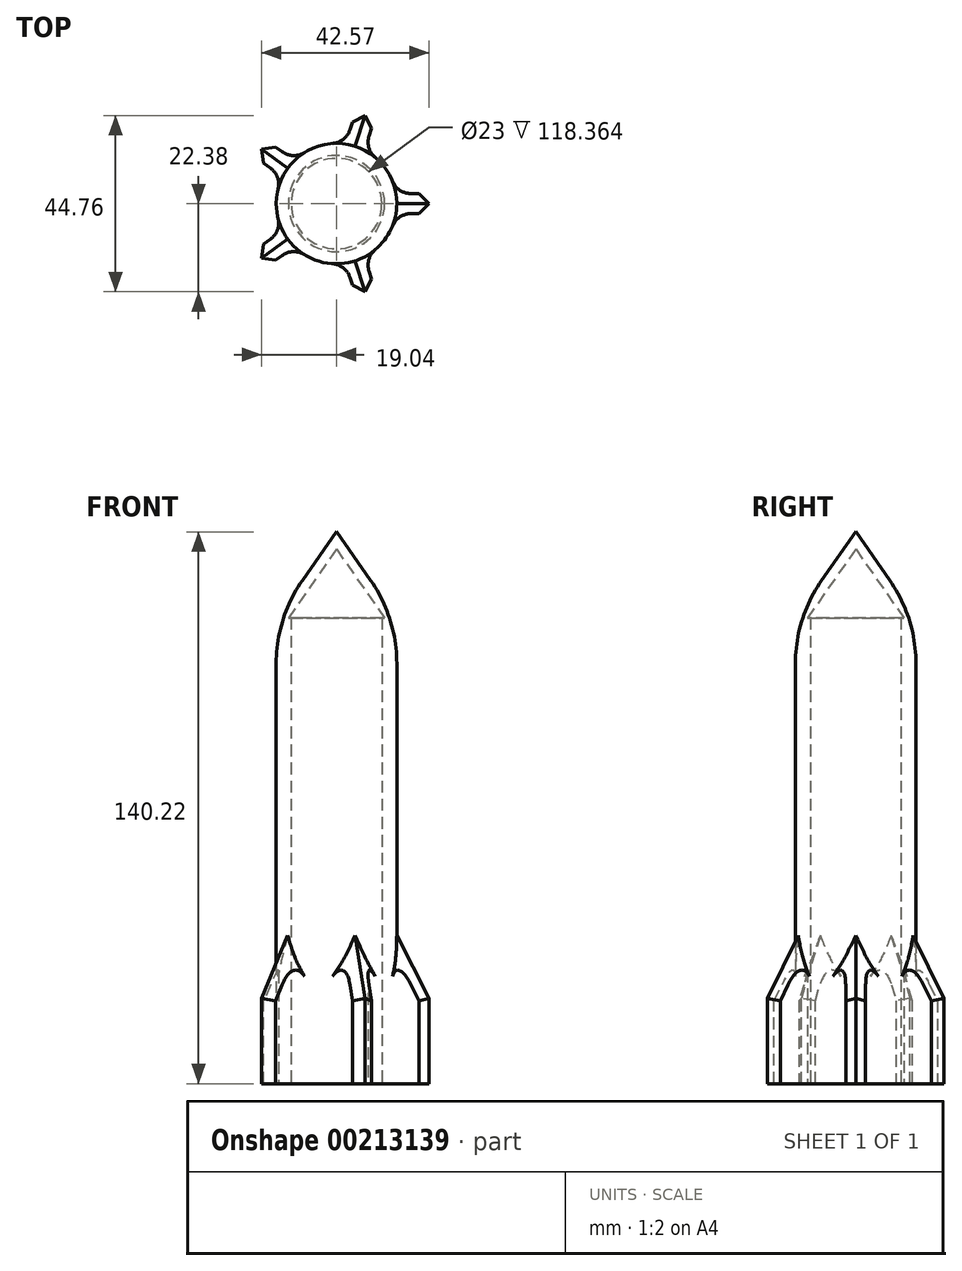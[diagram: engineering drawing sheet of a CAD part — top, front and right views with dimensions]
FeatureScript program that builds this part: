
annotation { "Feature Type Name" : "Feature", "Feature Type Description" : "" }
export const myFeature = defineFeature(function(context is Context, id is Id, definition is map)
    precondition{}
    {
        {
            var Q0;
            Q0=qCreatedBy(makeId("Top.planeOp"),FACE);
            var sketch = newSketch(context, id + "F0", { "sketchPlane" : qUnion([Q0])});
            skCircle(sketch, "E0", {"center": v(0, 0) * mm, "radius": 11.5 * mm});
            skCircle(sketch, "E1", {"center": v(0, 0) * mm, "radius": 15.3 * mm});
            skSolve(sketch);
        }
        {
            var Q0;
            Q0=makeQuery(id+"F0.imprint","IMPRINT",FACE,{"disambiguationData":[TD([[makeQuery(id+"F0.imprint","IMPRINT",EDGE,{"derivedFrom":sQuery(id+"F0.wireOp",EDGE,"E0")}),-1.0]])]});
            extrude(context, id + "F1", {"entities" : qUnion([Q0]), "depth" : 101.6 * mm});
        }
        {
            var Q0;
            Q0=makeQuery(id+"F1.opExtrude","CAP_FACE",FACE,{"disambiguationData":[OSD([sQuery(id+"F0.wireOp",EDGE,"E0"),sQuery(id+"F0.wireOp",EDGE,"E1")])],"isStart":false});
            extrude(context, id + "F2", {"entities" : qUnion([Q0]), "operationType" : NewBodyOperationType.ADD, "depth" : 25.4 * mm});
        }
        {
            var Q0;
            Q0=makeQuery(id+"F2.opExtrude","CAP_FACE",FACE,{"disambiguationData":[OSD([sQuery(id+"F0.wireOp",EDGE,"E0"),sQuery(id+"F0.wireOp",EDGE,"E1")])],"isStart":false});
            extrude(context, id + "F3", {"entities" : qUnion([Q0]), "operationType" : NewBodyOperationType.REMOVE, "oppositeDirection" : true, "depth" : 25.4 * mm});
        }
        {
            var Q0;
            Q0=makeQuery(id+"F3.boolean.opBoolean","COPY",FACE,{"derivedFrom":makeQuery(id+"F3.opExtrude","CAP_FACE",FACE,{"disambiguationData":[OSD([sQuery(id+"F0.wireOp",EDGE,"E0"),sQuery(id+"F0.wireOp",EDGE,"E1")])],"isStart":false})});
            extrude(context, id + "F4", {"entities" : qUnion([Q0]), "operationType" : NewBodyOperationType.ADD, "depth" : 25.4 * mm});
        }
        {
            var Q0;
            Q0=makeQuery(id+"F4.opExtrude","CAP_FACE",FACE,{"disambiguationData":[OSD([sQuery(id+"F0.wireOp",EDGE,"E0"),sQuery(id+"F0.wireOp",EDGE,"E1")])],"isStart":false});
            extrude(context, id + "F5", {"entities" : qUnion([Q0]), "operationType" : NewBodyOperationType.REMOVE, "oppositeDirection" : true, "depth" : 25.4 * mm});
        }
        {
            var Q0;
            Q0=makeQuery(id+"F5.boolean.opBoolean","COPY",FACE,{"derivedFrom":makeQuery(id+"F5.opExtrude","CAP_FACE",FACE,{"disambiguationData":[OSD([sQuery(id+"F0.wireOp",EDGE,"E0"),sQuery(id+"F0.wireOp",EDGE,"E1")])],"isStart":false})});
            var sketch = newSketch(context, id + "F6", { "sketchPlane" : qUnion([Q0])});
            skCircle(sketch, "E2.0", {"center": v(0, 0) * mm, "radius": 15.3 * mm});
            skSolve(sketch);
        }
        {
            var Q0;
            Q0 = qSketchRegion(id + "F6", true);
            extrude(context, id + "F7", {"entities" : qUnion([Q0]), "operationType" : NewBodyOperationType.ADD, "depth" : 25.4 * mm, "hasDraft" : true, "draftAngle" : 35 * degree, "draftPullDirection" : true});
        }
        {
            var Q0;
            Q0=makeQuery(id+"F7.opExtrude","CAP_FACE",FACE,{"disambiguationData":[OSD([sQuery(id+"F6.wireOp",EDGE,"E2.0")])],"isStart":true});
            shell(context, id + "F8", {"entities" : qUnion([Q0]), "thickness" : 2.54 * mm});
        }
        {
            var Q0;
            Q0=qCreatedBy(makeId("Front.planeOp"),FACE);
            var sketch = newSketch(context, id + "F9", { "sketchPlane" : qUnion([Q0])});
            skLineSegment(sketch, "E3", {"start": v(12.54, 26.28) * mm, "end": v(26.07, 0) * mm});
            skLineSegment(sketch, "E4", {"start": v(26.07, 0) * mm, "end": v(12.7, 0) * mm});
            skLineSegment(sketch, "E5", {"start": v(12.7, 0) * mm, "end": v(12.54, 26.28) * mm});
            skSolve(sketch);
        }
        {
            var Q0;
            Q0 = qSketchRegion(id + "F9", true);
            extrude(context, id + "F10", {"entities" : qUnion([Q0]), "operationType" : NewBodyOperationType.ADD, "endBound" : BoundingType.SYMMETRIC, "depth" : 5.08 * mm});
        }
        {
            var Q0;
            Q0=makeQuery(id+"F10.boolean.opBoolean","MERGE",FACE,{"derivedFrom":[makeQuery(id+"F1.opExtrude","CAP_FACE",FACE,{"disambiguationData":[OSD([sQuery(id+"F0.wireOp",EDGE,"E0"),sQuery(id+"F0.wireOp",EDGE,"E1")])],"isStart":true}),makeQuery(id+"F10.opExtrude","SWEPT_FACE",FACE,{"disambiguationData":[OSD([sQuery(id+"F9.wireOp",EDGE,"E4")])]})]});
            extrude(context, id + "F11", {"entities" : qUnion([Q0]), "operationType" : NewBodyOperationType.ADD, "depth" : 10.67 * mm});
        }
        {
            var Q0;
            Q0=makeQuery(id+"F1.opExtrude","SWEPT_BODY",BODY,{"disambiguationData":[OSD([sQuery(id+"F0.wireOp",EDGE,"E0"),sQuery(id+"F0.wireOp",EDGE,"E1")])]});
            var Q1;
            {var subQ0=sQuery(id+"F0.wireOp",EDGE,"E0");Q1=makeQuery(id+"F11.boolean.opBoolean","MERGE",FACE,{"derivedFrom":[makeQuery(id+"F4.boolean.opBoolean","MERGE",FACE,{"derivedFrom":[makeQuery(id+"F2.boolean.opBoolean","MERGE",FACE,{"derivedFrom":[makeQuery(id+"F1.opExtrude","SWEPT_FACE",FACE,{"disambiguationData":[OSD([subQ0])]}),makeQuery(id+"F2.opExtrude","SWEPT_FACE",FACE,{"disambiguationData":[OSD([subQ0])]})]}),makeQuery(id+"F4.opExtrude","SWEPT_FACE",FACE,{"disambiguationData":[OSD([subQ0])]})]}),makeQuery(id+"F11.opExtrude","SWEPT_FACE",FACE,{"disambiguationData":[OSD([subQ0])]})]});}
            circularPattern(context, id + "F12", {"entities" : qUnion([Q0]), "axis" : qUnion([Q1]), "angle" : 360 * degree, "instanceCount" : 5, "equalSpace" : true});
        }
        {
            var Q0;
            Q0=makeQuery(id+"F12.opPattern","COPY",BODY,{"derivedFrom":makeQuery(id+"F1.opExtrude","SWEPT_BODY",BODY,{"disambiguationData":[OSD([sQuery(id+"F0.wireOp",EDGE,"E0"),sQuery(id+"F0.wireOp",EDGE,"E1")])]}),"instanceName":"2"});
            var Q1;
            Q1=makeQuery(id+"F12.opPattern","COPY",BODY,{"derivedFrom":makeQuery(id+"F1.opExtrude","SWEPT_BODY",BODY,{"disambiguationData":[OSD([sQuery(id+"F0.wireOp",EDGE,"E0"),sQuery(id+"F0.wireOp",EDGE,"E1")])]}),"instanceName":"1"});
            var Q2;
            Q2=makeQuery(id+"F1.opExtrude","SWEPT_BODY",BODY,{"disambiguationData":[OSD([sQuery(id+"F0.wireOp",EDGE,"E0"),sQuery(id+"F0.wireOp",EDGE,"E1")])]});
            var Q3;
            Q3=makeQuery(id+"F12.opPattern","COPY",BODY,{"derivedFrom":makeQuery(id+"F1.opExtrude","SWEPT_BODY",BODY,{"disambiguationData":[OSD([sQuery(id+"F0.wireOp",EDGE,"E0"),sQuery(id+"F0.wireOp",EDGE,"E1")])]}),"instanceName":"4"});
            var Q4;
            Q4=makeQuery(id+"F12.opPattern","COPY",BODY,{"derivedFrom":makeQuery(id+"F1.opExtrude","SWEPT_BODY",BODY,{"disambiguationData":[OSD([sQuery(id+"F0.wireOp",EDGE,"E0"),sQuery(id+"F0.wireOp",EDGE,"E1")])]}),"instanceName":"3"});
            booleanBodies(context, id + "F13", {"operationType" : BooleanOperationType.UNION, "tools" : qUnion([Q0, Q1, Q2, Q3, Q4])});
        }
        {
            var Q0;
            Q0=makeQuery(id+"F10.opExtrude","CAP_EDGE",EDGE,{"disambiguationData":[OSD([sQuery(id+"F9.wireOp",EDGE,"E3")])],"isStart":true});
            var Q1;
            Q1=makeQuery(id+"F10.opExtrude","CAP_EDGE",EDGE,{"disambiguationData":[OSD([sQuery(id+"F9.wireOp",EDGE,"E3")])],"isStart":false});
            var Q2;
            Q2=makeQuery(id+"F12.opPattern","COPY",EDGE,{"derivedFrom":makeQuery(id+"F10.opExtrude","CAP_EDGE",EDGE,{"disambiguationData":[OSD([sQuery(id+"F9.wireOp",EDGE,"E3")])],"isStart":false}),"instanceName":"1"});
            var Q3;
            Q3=makeQuery(id+"F12.opPattern","COPY",EDGE,{"derivedFrom":makeQuery(id+"F10.opExtrude","CAP_EDGE",EDGE,{"disambiguationData":[OSD([sQuery(id+"F9.wireOp",EDGE,"E3")])],"isStart":true}),"instanceName":"1"});
            var Q4;
            Q4=makeQuery(id+"F12.opPattern","COPY",EDGE,{"derivedFrom":makeQuery(id+"F10.opExtrude","CAP_EDGE",EDGE,{"disambiguationData":[OSD([sQuery(id+"F9.wireOp",EDGE,"E3")])],"isStart":false}),"instanceName":"2"});
            var Q5;
            Q5=makeQuery(id+"F12.opPattern","COPY",EDGE,{"derivedFrom":makeQuery(id+"F10.opExtrude","CAP_EDGE",EDGE,{"disambiguationData":[OSD([sQuery(id+"F9.wireOp",EDGE,"E3")])],"isStart":true}),"instanceName":"2"});
            var Q6;
            Q6=makeQuery(id+"F12.opPattern","COPY",EDGE,{"derivedFrom":makeQuery(id+"F10.opExtrude","CAP_EDGE",EDGE,{"disambiguationData":[OSD([sQuery(id+"F9.wireOp",EDGE,"E3")])],"isStart":false}),"instanceName":"3"});
            var Q7;
            Q7=makeQuery(id+"F12.opPattern","COPY",EDGE,{"derivedFrom":makeQuery(id+"F10.opExtrude","CAP_EDGE",EDGE,{"disambiguationData":[OSD([sQuery(id+"F9.wireOp",EDGE,"E3")])],"isStart":true}),"instanceName":"3"});
            var Q8;
            Q8=makeQuery(id+"F12.opPattern","COPY",EDGE,{"derivedFrom":makeQuery(id+"F10.opExtrude","CAP_EDGE",EDGE,{"disambiguationData":[OSD([sQuery(id+"F9.wireOp",EDGE,"E3")])],"isStart":true}),"instanceName":"4"});
            var Q9;
            Q9=makeQuery(id+"F12.opPattern","COPY",EDGE,{"derivedFrom":makeQuery(id+"F10.opExtrude","CAP_EDGE",EDGE,{"disambiguationData":[OSD([sQuery(id+"F9.wireOp",EDGE,"E3")])],"isStart":false}),"instanceName":"4"});
            chamfer(context, id + "F14", {"entities" : qUnion([Q0, Q1, Q2, Q3, Q4, Q5, Q6, Q7, Q8, Q9]), "width" : 2.54 * mm, "tangentPropagation" : true});
        }
        {
            var Q0;
            {var subQ0=makeQuery(id+"F11.opExtrude","CAP_FACE",FACE,{"disambiguationData":[OSD([sQuery(id+"F0.wireOp",EDGE,"E0"),sQuery(id+"F0.wireOp",EDGE,"E1"),sQuery(id+"F9.wireOp",EDGE,"E4")])],"isStart":false});Q0=makeQuery(id+"F13.opBoolean","MERGE",FACE,{"derivedFrom":[subQ0,makeQuery(id+"F12.opPattern","COPY",FACE,{"derivedFrom":subQ0,"instanceName":"1"}),makeQuery(id+"F12.opPattern","COPY",FACE,{"derivedFrom":subQ0,"instanceName":"2"}),makeQuery(id+"F12.opPattern","COPY",FACE,{"derivedFrom":subQ0,"instanceName":"3"}),makeQuery(id+"F12.opPattern","COPY",FACE,{"derivedFrom":subQ0,"instanceName":"4"})]});}
            extrude(context, id + "F15", {"entities" : qUnion([Q0]), "operationType" : NewBodyOperationType.ADD, "depth" : 25.4 * mm});
        }
        {
            var Q0;
            {var subQ0=sQuery(id+"F9.wireOp",EDGE,"E4");var subQ1=sQuery(id+"F9.wireOp",EDGE,"E3");var subQ2=makeQuery(id+"F10.opExtrude","CAP_VERTEX",VERTEX,{"disambiguationData":[OSD([subQ1,subQ0])],"isStart":false});Q0=makeQuery(id+"F15.boolean.opBoolean","MERGE",EDGE,{"derivedFrom":[makeQuery(id+"F12.opPattern","COPY",EDGE,{"derivedFrom":makeQuery(id+"F11.opExtrude","SWEPT_EDGE",EDGE,{"disambiguationData":[OSD([subQ1,subQ0]),TDD([subQ2])]}),"instanceName":"2"}),makeQuery(id+"F15.opExtrude","SWEPT_EDGE",EDGE,{"disambiguationData":[OSD([subQ1,subQ0]),TDD([makeQuery(id+"F12.opPattern","COPY",VERTEX,{"derivedFrom":makeQuery(id+"F11.opExtrude","CAP_VERTEX",VERTEX,{"disambiguationData":[OSD([subQ1,subQ0]),TDD([subQ2])],"isStart":false}),"instanceName":"2"})])]})]});}
            var Q1;
            {var subQ0=sQuery(id+"F9.wireOp",EDGE,"E4");var subQ1=sQuery(id+"F9.wireOp",EDGE,"E3");var subQ2=makeQuery(id+"F10.opExtrude","CAP_VERTEX",VERTEX,{"disambiguationData":[OSD([subQ1,subQ0])],"isStart":true});Q1=makeQuery(id+"F15.boolean.opBoolean","MERGE",EDGE,{"derivedFrom":[makeQuery(id+"F12.opPattern","COPY",EDGE,{"derivedFrom":makeQuery(id+"F11.opExtrude","SWEPT_EDGE",EDGE,{"disambiguationData":[OSD([subQ1,subQ0]),TDD([subQ2])]}),"instanceName":"2"}),makeQuery(id+"F15.opExtrude","SWEPT_EDGE",EDGE,{"disambiguationData":[OSD([subQ1,subQ0]),TDD([makeQuery(id+"F12.opPattern","COPY",VERTEX,{"derivedFrom":makeQuery(id+"F11.opExtrude","CAP_VERTEX",VERTEX,{"disambiguationData":[OSD([subQ1,subQ0]),TDD([subQ2])],"isStart":false}),"instanceName":"2"})])]})]});}
            var Q2;
            {var subQ0=sQuery(id+"F9.wireOp",EDGE,"E4");var subQ1=sQuery(id+"F9.wireOp",EDGE,"E3");var subQ2=makeQuery(id+"F10.opExtrude","CAP_VERTEX",VERTEX,{"disambiguationData":[OSD([subQ1,subQ0])],"isStart":true});Q2=makeQuery(id+"F15.boolean.opBoolean","MERGE",EDGE,{"derivedFrom":[makeQuery(id+"F12.opPattern","COPY",EDGE,{"derivedFrom":makeQuery(id+"F11.opExtrude","SWEPT_EDGE",EDGE,{"disambiguationData":[OSD([subQ1,subQ0]),TDD([subQ2])]}),"instanceName":"3"}),makeQuery(id+"F15.opExtrude","SWEPT_EDGE",EDGE,{"disambiguationData":[OSD([subQ1,subQ0]),TDD([makeQuery(id+"F12.opPattern","COPY",VERTEX,{"derivedFrom":makeQuery(id+"F11.opExtrude","CAP_VERTEX",VERTEX,{"disambiguationData":[OSD([subQ1,subQ0]),TDD([subQ2])],"isStart":false}),"instanceName":"3"})])]})]});}
            var Q3;
            {var subQ0=sQuery(id+"F9.wireOp",EDGE,"E4");var subQ1=sQuery(id+"F9.wireOp",EDGE,"E3");var subQ2=makeQuery(id+"F10.opExtrude","CAP_VERTEX",VERTEX,{"disambiguationData":[OSD([subQ1,subQ0])],"isStart":false});Q3=makeQuery(id+"F15.boolean.opBoolean","MERGE",EDGE,{"derivedFrom":[makeQuery(id+"F12.opPattern","COPY",EDGE,{"derivedFrom":makeQuery(id+"F11.opExtrude","SWEPT_EDGE",EDGE,{"disambiguationData":[OSD([subQ1,subQ0]),TDD([subQ2])]}),"instanceName":"3"}),makeQuery(id+"F15.opExtrude","SWEPT_EDGE",EDGE,{"disambiguationData":[OSD([subQ1,subQ0]),TDD([makeQuery(id+"F12.opPattern","COPY",VERTEX,{"derivedFrom":makeQuery(id+"F11.opExtrude","CAP_VERTEX",VERTEX,{"disambiguationData":[OSD([subQ1,subQ0]),TDD([subQ2])],"isStart":false}),"instanceName":"3"})])]})]});}
            var Q4;
            {var subQ0=sQuery(id+"F9.wireOp",EDGE,"E4");var subQ1=sQuery(id+"F9.wireOp",EDGE,"E3");var subQ2=makeQuery(id+"F10.opExtrude","CAP_VERTEX",VERTEX,{"disambiguationData":[OSD([subQ1,subQ0])],"isStart":true});Q4=makeQuery(id+"F15.boolean.opBoolean","MERGE",EDGE,{"derivedFrom":[makeQuery(id+"F12.opPattern","COPY",EDGE,{"derivedFrom":makeQuery(id+"F11.opExtrude","SWEPT_EDGE",EDGE,{"disambiguationData":[OSD([subQ1,subQ0]),TDD([subQ2])]}),"instanceName":"4"}),makeQuery(id+"F15.opExtrude","SWEPT_EDGE",EDGE,{"disambiguationData":[OSD([subQ1,subQ0]),TDD([makeQuery(id+"F12.opPattern","COPY",VERTEX,{"derivedFrom":makeQuery(id+"F11.opExtrude","CAP_VERTEX",VERTEX,{"disambiguationData":[OSD([subQ1,subQ0]),TDD([subQ2])],"isStart":false}),"instanceName":"4"})])]})]});}
            var Q5;
            {var subQ0=sQuery(id+"F9.wireOp",EDGE,"E4");var subQ1=sQuery(id+"F9.wireOp",EDGE,"E3");var subQ2=makeQuery(id+"F10.opExtrude","CAP_VERTEX",VERTEX,{"disambiguationData":[OSD([subQ1,subQ0])],"isStart":false});Q5=makeQuery(id+"F15.boolean.opBoolean","MERGE",EDGE,{"derivedFrom":[makeQuery(id+"F12.opPattern","COPY",EDGE,{"derivedFrom":makeQuery(id+"F11.opExtrude","SWEPT_EDGE",EDGE,{"disambiguationData":[OSD([subQ1,subQ0]),TDD([subQ2])]}),"instanceName":"4"}),makeQuery(id+"F15.opExtrude","SWEPT_EDGE",EDGE,{"disambiguationData":[OSD([subQ1,subQ0]),TDD([makeQuery(id+"F12.opPattern","COPY",VERTEX,{"derivedFrom":makeQuery(id+"F11.opExtrude","CAP_VERTEX",VERTEX,{"disambiguationData":[OSD([subQ1,subQ0]),TDD([subQ2])],"isStart":false}),"instanceName":"4"})])]})]});}
            var Q6;
            {var subQ0=sQuery(id+"F9.wireOp",EDGE,"E4");var subQ1=sQuery(id+"F9.wireOp",EDGE,"E3");var subQ2=makeQuery(id+"F10.opExtrude","CAP_VERTEX",VERTEX,{"disambiguationData":[OSD([subQ1,subQ0])],"isStart":false});Q6=makeQuery(id+"F15.boolean.opBoolean","MERGE",EDGE,{"derivedFrom":[makeQuery(id+"F11.opExtrude","SWEPT_EDGE",EDGE,{"disambiguationData":[OSD([subQ1,subQ0]),TDD([subQ2])]}),makeQuery(id+"F15.opExtrude","SWEPT_EDGE",EDGE,{"disambiguationData":[OSD([subQ1,subQ0]),TDD([makeQuery(id+"F11.opExtrude","CAP_VERTEX",VERTEX,{"disambiguationData":[OSD([subQ1,subQ0]),TDD([subQ2])],"isStart":false})])]})]});}
            var Q7;
            {var subQ0=sQuery(id+"F9.wireOp",EDGE,"E4");var subQ1=sQuery(id+"F9.wireOp",EDGE,"E3");var subQ2=makeQuery(id+"F10.opExtrude","CAP_VERTEX",VERTEX,{"disambiguationData":[OSD([subQ1,subQ0])],"isStart":true});Q7=makeQuery(id+"F15.boolean.opBoolean","MERGE",EDGE,{"derivedFrom":[makeQuery(id+"F11.opExtrude","SWEPT_EDGE",EDGE,{"disambiguationData":[OSD([subQ1,subQ0]),TDD([subQ2])]}),makeQuery(id+"F15.opExtrude","SWEPT_EDGE",EDGE,{"disambiguationData":[OSD([subQ1,subQ0]),TDD([makeQuery(id+"F11.opExtrude","CAP_VERTEX",VERTEX,{"disambiguationData":[OSD([subQ1,subQ0]),TDD([subQ2])],"isStart":false})])]})]});}
            var Q8;
            {var subQ0=sQuery(id+"F9.wireOp",EDGE,"E4");var subQ1=sQuery(id+"F9.wireOp",EDGE,"E3");var subQ2=makeQuery(id+"F10.opExtrude","CAP_VERTEX",VERTEX,{"disambiguationData":[OSD([subQ1,subQ0])],"isStart":true});Q8=makeQuery(id+"F15.boolean.opBoolean","MERGE",EDGE,{"derivedFrom":[makeQuery(id+"F12.opPattern","COPY",EDGE,{"derivedFrom":makeQuery(id+"F11.opExtrude","SWEPT_EDGE",EDGE,{"disambiguationData":[OSD([subQ1,subQ0]),TDD([subQ2])]}),"instanceName":"1"}),makeQuery(id+"F15.opExtrude","SWEPT_EDGE",EDGE,{"disambiguationData":[OSD([subQ1,subQ0]),TDD([makeQuery(id+"F12.opPattern","COPY",VERTEX,{"derivedFrom":makeQuery(id+"F11.opExtrude","CAP_VERTEX",VERTEX,{"disambiguationData":[OSD([subQ1,subQ0]),TDD([subQ2])],"isStart":false}),"instanceName":"1"})])]})]});}
            var Q9;
            {var subQ0=sQuery(id+"F9.wireOp",EDGE,"E4");var subQ1=sQuery(id+"F9.wireOp",EDGE,"E3");var subQ2=makeQuery(id+"F10.opExtrude","CAP_VERTEX",VERTEX,{"disambiguationData":[OSD([subQ1,subQ0])],"isStart":false});Q9=makeQuery(id+"F15.boolean.opBoolean","MERGE",EDGE,{"derivedFrom":[makeQuery(id+"F12.opPattern","COPY",EDGE,{"derivedFrom":makeQuery(id+"F11.opExtrude","SWEPT_EDGE",EDGE,{"disambiguationData":[OSD([subQ1,subQ0]),TDD([subQ2])]}),"instanceName":"1"}),makeQuery(id+"F15.opExtrude","SWEPT_EDGE",EDGE,{"disambiguationData":[OSD([subQ1,subQ0]),TDD([makeQuery(id+"F12.opPattern","COPY",VERTEX,{"derivedFrom":makeQuery(id+"F11.opExtrude","CAP_VERTEX",VERTEX,{"disambiguationData":[OSD([subQ1,subQ0]),TDD([subQ2])],"isStart":false}),"instanceName":"1"})])]})]});}
            chamfer(context, id + "F16", {"entities" : qUnion([Q0, Q1, Q2, Q3, Q4, Q5, Q6, Q7, Q8, Q9]), "width" : 5.08 * mm, "tangentPropagation" : true});
        }
        {
            var Q0;
            Q0=makeQuery(id+"F15.opExtrude","CAP_FACE",FACE,{"disambiguationData":[OSD([sQuery(id+"F0.wireOp",EDGE,"E0"),sQuery(id+"F0.wireOp",EDGE,"E1"),sQuery(id+"F9.wireOp",EDGE,"E4")])],"isStart":false});
            extrude(context, id + "F17", {"entities" : qUnion([Q0]), "operationType" : NewBodyOperationType.REMOVE, "oppositeDirection" : true, "depth" : 19.3 * mm});
        }
        {
            var Q0;
            Q0=makeQuery(id+"F12.opPattern","COPY",EDGE,{"derivedFrom":makeQuery(id+"F7.boolean.opBoolean","MERGE",EDGE,{"derivedFrom":[makeQuery(id+"F5.boolean.opBoolean","COPY",EDGE,{"derivedFrom":makeQuery(id+"F5.opExtrude","CAP_EDGE",EDGE,{"disambiguationData":[OSD([sQuery(id+"F0.wireOp",EDGE,"E1")])],"isStart":false})}),makeQuery(id+"F7.opExtrude","CAP_EDGE",EDGE,{"disambiguationData":[OSD([sQuery(id+"F6.wireOp",EDGE,"E2.0")])],"isStart":true})]}),"instanceName":"2"});
            fillet(context, id + "F18", {"entities" : qUnion([Q0]), "radius" : 36.64 * mm, "tangentPropagation" : true, "allowEdgeOverflow" : false});
        }
        {
            var Q0;
            {var subQ0=sQuery(id+"F9.wireOp",EDGE,"E5");var subQ1=sQuery(id+"F9.wireOp",EDGE,"E4");var subQ2=sQuery(id+"F9.wireOp",EDGE,"E3");var subQ3=sQuery(id+"F0.wireOp",EDGE,"E1");var subQ4=makeQuery(id+"F4.boolean.opBoolean","MERGE",FACE,{"derivedFrom":[makeQuery(id+"F2.boolean.opBoolean","MERGE",FACE,{"derivedFrom":[makeQuery(id+"F1.opExtrude","SWEPT_FACE",FACE,{"disambiguationData":[OSD([subQ3])]}),makeQuery(id+"F2.opExtrude","SWEPT_FACE",FACE,{"disambiguationData":[OSD([subQ3])]})]}),makeQuery(id+"F4.opExtrude","SWEPT_FACE",FACE,{"disambiguationData":[OSD([subQ3])]})]});var subQ5=makeQuery(id+"F11.boolean.opBoolean","MERGE",FACE,{"derivedFrom":[subQ4,makeQuery(id+"F11.opExtrude","SWEPT_FACE",FACE,{"disambiguationData":[OSD([subQ3])]})]});Q0=makeQuery(id+"F15.boolean.opBoolean","MERGE",EDGE,{"derivedFrom":[makeQuery(id+"F13.opBoolean","INTERSECT",EDGE,{"disambiguationData":[OD(2.0)],"derivedFrom":[subQ5,makeQuery(id+"F12.opPattern","COPY",FACE,{"derivedFrom":subQ5,"instanceName":"1"}),makeQuery(id+"F12.opPattern","COPY",FACE,{"derivedFrom":subQ5,"instanceName":"2"}),makeQuery(id+"F12.opPattern","COPY",FACE,{"derivedFrom":subQ5,"instanceName":"4"})]}),makeQuery(id+"F15.opExtrude","SWEPT_EDGE",EDGE,{"disambiguationData":[OSD([subQ3,subQ2,subQ1,subQ0]),TDD([makeQuery(id+"F12.opPattern","COPY",VERTEX,{"derivedFrom":makeQuery(id+"F11.opExtrude","CAP_VERTEX",VERTEX,{"disambiguationData":[OSD([subQ3,subQ2,subQ1,subQ0]),TDD([makeQuery(id+"F10.boolean.opBoolean","INTERSECT",VERTEX,{"derivedFrom":[subQ4,makeQuery(id+"F10.opExtrude","CAP_FACE",FACE,{"disambiguationData":[OSD([subQ2,subQ1,subQ0])],"isStart":false})]})])],"isStart":false}),"instanceName":"3"})])]})]});}
            var Q1;
            {var subQ0=sQuery(id+"F9.wireOp",EDGE,"E5");var subQ1=sQuery(id+"F9.wireOp",EDGE,"E4");var subQ2=sQuery(id+"F9.wireOp",EDGE,"E3");var subQ3=makeQuery(id+"F10.opExtrude","CAP_FACE",FACE,{"disambiguationData":[OSD([subQ2,subQ1,subQ0])],"isStart":true});var subQ4=sQuery(id+"F0.wireOp",EDGE,"E1");var subQ5=makeQuery(id+"F4.boolean.opBoolean","MERGE",FACE,{"derivedFrom":[makeQuery(id+"F2.boolean.opBoolean","MERGE",FACE,{"derivedFrom":[makeQuery(id+"F1.opExtrude","SWEPT_FACE",FACE,{"disambiguationData":[OSD([subQ4])]}),makeQuery(id+"F2.opExtrude","SWEPT_FACE",FACE,{"disambiguationData":[OSD([subQ4])]})]}),makeQuery(id+"F4.opExtrude","SWEPT_FACE",FACE,{"disambiguationData":[OSD([subQ4])]})]});var subQ6=makeQuery(id+"F10.boolean.opBoolean","INTERSECT",VERTEX,{"derivedFrom":[subQ5,subQ3]});Q1=makeQuery(id+"F15.boolean.opBoolean","MERGE",EDGE,{"derivedFrom":[makeQuery(id+"F12.opPattern","COPY",EDGE,{"derivedFrom":makeQuery(id+"F11.boolean.opBoolean","MERGE",EDGE,{"derivedFrom":[makeQuery(id+"F10.boolean.opBoolean","INTERSECT",EDGE,{"derivedFrom":[subQ5,subQ3]}),makeQuery(id+"F11.opExtrude","SWEPT_EDGE",EDGE,{"disambiguationData":[OSD([subQ4,subQ2,subQ1,subQ0]),TDD([subQ6])]})]}),"instanceName":"2"}),makeQuery(id+"F15.opExtrude","SWEPT_EDGE",EDGE,{"disambiguationData":[OSD([subQ4,subQ2,subQ1,subQ0]),TDD([makeQuery(id+"F12.opPattern","COPY",VERTEX,{"derivedFrom":makeQuery(id+"F11.opExtrude","CAP_VERTEX",VERTEX,{"disambiguationData":[OSD([subQ4,subQ2,subQ1,subQ0]),TDD([subQ6])],"isStart":false}),"instanceName":"2"})])]})]});}
            var Q2;
            {var subQ0=sQuery(id+"F9.wireOp",EDGE,"E5");var subQ1=sQuery(id+"F9.wireOp",EDGE,"E4");var subQ2=sQuery(id+"F9.wireOp",EDGE,"E3");var subQ3=makeQuery(id+"F10.opExtrude","CAP_FACE",FACE,{"disambiguationData":[OSD([subQ2,subQ1,subQ0])],"isStart":false});var subQ4=sQuery(id+"F0.wireOp",EDGE,"E1");var subQ5=makeQuery(id+"F4.boolean.opBoolean","MERGE",FACE,{"derivedFrom":[makeQuery(id+"F2.boolean.opBoolean","MERGE",FACE,{"derivedFrom":[makeQuery(id+"F1.opExtrude","SWEPT_FACE",FACE,{"disambiguationData":[OSD([subQ4])]}),makeQuery(id+"F2.opExtrude","SWEPT_FACE",FACE,{"disambiguationData":[OSD([subQ4])]})]}),makeQuery(id+"F4.opExtrude","SWEPT_FACE",FACE,{"disambiguationData":[OSD([subQ4])]})]});var subQ6=makeQuery(id+"F10.boolean.opBoolean","INTERSECT",VERTEX,{"derivedFrom":[subQ5,subQ3]});Q2=makeQuery(id+"F15.boolean.opBoolean","MERGE",EDGE,{"derivedFrom":[makeQuery(id+"F12.opPattern","COPY",EDGE,{"derivedFrom":makeQuery(id+"F11.boolean.opBoolean","MERGE",EDGE,{"derivedFrom":[makeQuery(id+"F10.boolean.opBoolean","INTERSECT",EDGE,{"derivedFrom":[subQ5,subQ3]}),makeQuery(id+"F11.opExtrude","SWEPT_EDGE",EDGE,{"disambiguationData":[OSD([subQ4,subQ2,subQ1,subQ0]),TDD([subQ6])]})]}),"instanceName":"2"}),makeQuery(id+"F15.opExtrude","SWEPT_EDGE",EDGE,{"disambiguationData":[OSD([subQ4,subQ2,subQ1,subQ0]),TDD([makeQuery(id+"F12.opPattern","COPY",VERTEX,{"derivedFrom":makeQuery(id+"F11.opExtrude","CAP_VERTEX",VERTEX,{"disambiguationData":[OSD([subQ4,subQ2,subQ1,subQ0]),TDD([subQ6])],"isStart":false}),"instanceName":"2"})])]})]});}
            var Q3;
            {var subQ0=sQuery(id+"F9.wireOp",EDGE,"E5");var subQ1=sQuery(id+"F9.wireOp",EDGE,"E4");var subQ2=sQuery(id+"F9.wireOp",EDGE,"E3");var subQ3=sQuery(id+"F0.wireOp",EDGE,"E1");var subQ4=makeQuery(id+"F4.boolean.opBoolean","MERGE",FACE,{"derivedFrom":[makeQuery(id+"F2.boolean.opBoolean","MERGE",FACE,{"derivedFrom":[makeQuery(id+"F1.opExtrude","SWEPT_FACE",FACE,{"disambiguationData":[OSD([subQ3])]}),makeQuery(id+"F2.opExtrude","SWEPT_FACE",FACE,{"disambiguationData":[OSD([subQ3])]})]}),makeQuery(id+"F4.opExtrude","SWEPT_FACE",FACE,{"disambiguationData":[OSD([subQ3])]})]});var subQ5=makeQuery(id+"F11.boolean.opBoolean","MERGE",FACE,{"derivedFrom":[subQ4,makeQuery(id+"F11.opExtrude","SWEPT_FACE",FACE,{"disambiguationData":[OSD([subQ3])]})]});Q3=makeQuery(id+"F15.boolean.opBoolean","MERGE",EDGE,{"derivedFrom":[makeQuery(id+"F13.opBoolean","INTERSECT",EDGE,{"disambiguationData":[OD(1.0)],"derivedFrom":[subQ5,makeQuery(id+"F12.opPattern","COPY",FACE,{"derivedFrom":subQ5,"instanceName":"2"})]}),makeQuery(id+"F15.opExtrude","SWEPT_EDGE",EDGE,{"disambiguationData":[OSD([subQ3,subQ2,subQ1,subQ0]),TDD([makeQuery(id+"F12.opPattern","COPY",VERTEX,{"derivedFrom":makeQuery(id+"F11.opExtrude","CAP_VERTEX",VERTEX,{"disambiguationData":[OSD([subQ3,subQ2,subQ1,subQ0]),TDD([makeQuery(id+"F10.boolean.opBoolean","INTERSECT",VERTEX,{"derivedFrom":[subQ4,makeQuery(id+"F10.opExtrude","CAP_FACE",FACE,{"disambiguationData":[OSD([subQ2,subQ1,subQ0])],"isStart":true})]})])],"isStart":false}),"instanceName":"1"})])]})]});}
            var Q4;
            {var subQ0=sQuery(id+"F9.wireOp",EDGE,"E5");var subQ1=sQuery(id+"F9.wireOp",EDGE,"E4");var subQ2=sQuery(id+"F9.wireOp",EDGE,"E3");var subQ3=sQuery(id+"F0.wireOp",EDGE,"E1");var subQ4=makeQuery(id+"F4.boolean.opBoolean","MERGE",FACE,{"derivedFrom":[makeQuery(id+"F2.boolean.opBoolean","MERGE",FACE,{"derivedFrom":[makeQuery(id+"F1.opExtrude","SWEPT_FACE",FACE,{"disambiguationData":[OSD([subQ3])]}),makeQuery(id+"F2.opExtrude","SWEPT_FACE",FACE,{"disambiguationData":[OSD([subQ3])]})]}),makeQuery(id+"F4.opExtrude","SWEPT_FACE",FACE,{"disambiguationData":[OSD([subQ3])]})]});var subQ5=makeQuery(id+"F11.boolean.opBoolean","MERGE",FACE,{"derivedFrom":[subQ4,makeQuery(id+"F11.opExtrude","SWEPT_FACE",FACE,{"disambiguationData":[OSD([subQ3])]})]});Q4=makeQuery(id+"F15.boolean.opBoolean","MERGE",EDGE,{"derivedFrom":[makeQuery(id+"F13.opBoolean","INTERSECT",EDGE,{"disambiguationData":[OD(2.0)],"derivedFrom":[subQ5,makeQuery(id+"F12.opPattern","COPY",FACE,{"derivedFrom":subQ5,"instanceName":"2"})]}),makeQuery(id+"F15.opExtrude","SWEPT_EDGE",EDGE,{"disambiguationData":[OSD([subQ3,subQ2,subQ1,subQ0]),TDD([makeQuery(id+"F12.opPattern","COPY",VERTEX,{"derivedFrom":makeQuery(id+"F11.opExtrude","CAP_VERTEX",VERTEX,{"disambiguationData":[OSD([subQ3,subQ2,subQ1,subQ0]),TDD([makeQuery(id+"F10.boolean.opBoolean","INTERSECT",VERTEX,{"derivedFrom":[subQ4,makeQuery(id+"F10.opExtrude","CAP_FACE",FACE,{"disambiguationData":[OSD([subQ2,subQ1,subQ0])],"isStart":false})]})])],"isStart":false}),"instanceName":"1"})])]})]});}
            var Q5;
            {var subQ0=sQuery(id+"F9.wireOp",EDGE,"E5");var subQ1=sQuery(id+"F9.wireOp",EDGE,"E4");var subQ2=sQuery(id+"F9.wireOp",EDGE,"E3");var subQ3=sQuery(id+"F0.wireOp",EDGE,"E1");var subQ4=makeQuery(id+"F4.boolean.opBoolean","MERGE",FACE,{"derivedFrom":[makeQuery(id+"F2.boolean.opBoolean","MERGE",FACE,{"derivedFrom":[makeQuery(id+"F1.opExtrude","SWEPT_FACE",FACE,{"disambiguationData":[OSD([subQ3])]}),makeQuery(id+"F2.opExtrude","SWEPT_FACE",FACE,{"disambiguationData":[OSD([subQ3])]})]}),makeQuery(id+"F4.opExtrude","SWEPT_FACE",FACE,{"disambiguationData":[OSD([subQ3])]})]});var subQ5=makeQuery(id+"F11.boolean.opBoolean","MERGE",FACE,{"derivedFrom":[subQ4,makeQuery(id+"F11.opExtrude","SWEPT_FACE",FACE,{"disambiguationData":[OSD([subQ3])]})]});Q5=makeQuery(id+"F15.boolean.opBoolean","MERGE",EDGE,{"derivedFrom":[makeQuery(id+"F13.opBoolean","INTERSECT",EDGE,{"disambiguationData":[OD(1.0)],"derivedFrom":[makeQuery(id+"F12.opPattern","COPY",FACE,{"derivedFrom":subQ5,"instanceName":"1"}),makeQuery(id+"F12.opPattern","COPY",FACE,{"derivedFrom":subQ5,"instanceName":"2"}),makeQuery(id+"F12.opPattern","COPY",FACE,{"derivedFrom":subQ5,"instanceName":"4"})]}),makeQuery(id+"F15.opExtrude","SWEPT_EDGE",EDGE,{"disambiguationData":[OSD([subQ3,subQ2,subQ1,subQ0]),TDD([makeQuery(id+"F11.opExtrude","CAP_VERTEX",VERTEX,{"disambiguationData":[OSD([subQ3,subQ2,subQ1,subQ0]),TDD([makeQuery(id+"F10.boolean.opBoolean","INTERSECT",VERTEX,{"derivedFrom":[subQ4,makeQuery(id+"F10.opExtrude","CAP_FACE",FACE,{"disambiguationData":[OSD([subQ2,subQ1,subQ0])],"isStart":true})]})])],"isStart":false})])]})]});}
            var Q6;
            {var subQ0=sQuery(id+"F9.wireOp",EDGE,"E5");var subQ1=sQuery(id+"F9.wireOp",EDGE,"E4");var subQ2=sQuery(id+"F9.wireOp",EDGE,"E3");var subQ3=sQuery(id+"F0.wireOp",EDGE,"E1");var subQ4=makeQuery(id+"F4.boolean.opBoolean","MERGE",FACE,{"derivedFrom":[makeQuery(id+"F2.boolean.opBoolean","MERGE",FACE,{"derivedFrom":[makeQuery(id+"F1.opExtrude","SWEPT_FACE",FACE,{"disambiguationData":[OSD([subQ3])]}),makeQuery(id+"F2.opExtrude","SWEPT_FACE",FACE,{"disambiguationData":[OSD([subQ3])]})]}),makeQuery(id+"F4.opExtrude","SWEPT_FACE",FACE,{"disambiguationData":[OSD([subQ3])]})]});var subQ5=makeQuery(id+"F11.boolean.opBoolean","MERGE",FACE,{"derivedFrom":[subQ4,makeQuery(id+"F11.opExtrude","SWEPT_FACE",FACE,{"disambiguationData":[OSD([subQ3])]})]});Q6=makeQuery(id+"F15.boolean.opBoolean","MERGE",EDGE,{"derivedFrom":[makeQuery(id+"F13.opBoolean","INTERSECT",EDGE,{"disambiguationData":[OD(2.0)],"derivedFrom":[makeQuery(id+"F12.opPattern","COPY",FACE,{"derivedFrom":subQ5,"instanceName":"1"}),makeQuery(id+"F12.opPattern","COPY",FACE,{"derivedFrom":subQ5,"instanceName":"2"}),makeQuery(id+"F12.opPattern","COPY",FACE,{"derivedFrom":subQ5,"instanceName":"4"})]}),makeQuery(id+"F15.opExtrude","SWEPT_EDGE",EDGE,{"disambiguationData":[OSD([subQ3,subQ2,subQ1,subQ0]),TDD([makeQuery(id+"F11.opExtrude","CAP_VERTEX",VERTEX,{"disambiguationData":[OSD([subQ3,subQ2,subQ1,subQ0]),TDD([makeQuery(id+"F10.boolean.opBoolean","INTERSECT",VERTEX,{"derivedFrom":[subQ4,makeQuery(id+"F10.opExtrude","CAP_FACE",FACE,{"disambiguationData":[OSD([subQ2,subQ1,subQ0])],"isStart":false})]})])],"isStart":false})])]})]});}
            var Q7;
            {var subQ0=sQuery(id+"F9.wireOp",EDGE,"E5");var subQ1=sQuery(id+"F9.wireOp",EDGE,"E4");var subQ2=sQuery(id+"F9.wireOp",EDGE,"E3");var subQ3=sQuery(id+"F0.wireOp",EDGE,"E1");var subQ4=makeQuery(id+"F4.boolean.opBoolean","MERGE",FACE,{"derivedFrom":[makeQuery(id+"F2.boolean.opBoolean","MERGE",FACE,{"derivedFrom":[makeQuery(id+"F1.opExtrude","SWEPT_FACE",FACE,{"disambiguationData":[OSD([subQ3])]}),makeQuery(id+"F2.opExtrude","SWEPT_FACE",FACE,{"disambiguationData":[OSD([subQ3])]})]}),makeQuery(id+"F4.opExtrude","SWEPT_FACE",FACE,{"disambiguationData":[OSD([subQ3])]})]});var subQ5=makeQuery(id+"F11.boolean.opBoolean","MERGE",FACE,{"derivedFrom":[subQ4,makeQuery(id+"F11.opExtrude","SWEPT_FACE",FACE,{"disambiguationData":[OSD([subQ3])]})]});Q7=makeQuery(id+"F15.boolean.opBoolean","MERGE",EDGE,{"derivedFrom":[makeQuery(id+"F13.opBoolean","INTERSECT",EDGE,{"disambiguationData":[OD(2.0)],"derivedFrom":[subQ5,makeQuery(id+"F12.opPattern","COPY",FACE,{"derivedFrom":subQ5,"instanceName":"1"}),makeQuery(id+"F12.opPattern","COPY",FACE,{"derivedFrom":subQ5,"instanceName":"2"}),makeQuery(id+"F12.opPattern","COPY",FACE,{"derivedFrom":subQ5,"instanceName":"3"})]}),makeQuery(id+"F15.opExtrude","SWEPT_EDGE",EDGE,{"disambiguationData":[OSD([subQ3,subQ2,subQ1,subQ0]),TDD([makeQuery(id+"F12.opPattern","COPY",VERTEX,{"derivedFrom":makeQuery(id+"F11.opExtrude","CAP_VERTEX",VERTEX,{"disambiguationData":[OSD([subQ3,subQ2,subQ1,subQ0]),TDD([makeQuery(id+"F10.boolean.opBoolean","INTERSECT",VERTEX,{"derivedFrom":[subQ4,makeQuery(id+"F10.opExtrude","CAP_FACE",FACE,{"disambiguationData":[OSD([subQ2,subQ1,subQ0])],"isStart":false})]})])],"isStart":false}),"instanceName":"4"})])]})]});}
            var Q8;
            {var subQ0=sQuery(id+"F9.wireOp",EDGE,"E5");var subQ1=sQuery(id+"F9.wireOp",EDGE,"E4");var subQ2=sQuery(id+"F9.wireOp",EDGE,"E3");var subQ3=sQuery(id+"F0.wireOp",EDGE,"E1");var subQ4=makeQuery(id+"F4.boolean.opBoolean","MERGE",FACE,{"derivedFrom":[makeQuery(id+"F2.boolean.opBoolean","MERGE",FACE,{"derivedFrom":[makeQuery(id+"F1.opExtrude","SWEPT_FACE",FACE,{"disambiguationData":[OSD([subQ3])]}),makeQuery(id+"F2.opExtrude","SWEPT_FACE",FACE,{"disambiguationData":[OSD([subQ3])]})]}),makeQuery(id+"F4.opExtrude","SWEPT_FACE",FACE,{"disambiguationData":[OSD([subQ3])]})]});var subQ5=makeQuery(id+"F11.boolean.opBoolean","MERGE",FACE,{"derivedFrom":[subQ4,makeQuery(id+"F11.opExtrude","SWEPT_FACE",FACE,{"disambiguationData":[OSD([subQ3])]})]});Q8=makeQuery(id+"F15.boolean.opBoolean","MERGE",EDGE,{"derivedFrom":[makeQuery(id+"F13.opBoolean","INTERSECT",EDGE,{"disambiguationData":[OD(1.0)],"derivedFrom":[subQ5,makeQuery(id+"F12.opPattern","COPY",FACE,{"derivedFrom":subQ5,"instanceName":"1"}),makeQuery(id+"F12.opPattern","COPY",FACE,{"derivedFrom":subQ5,"instanceName":"2"}),makeQuery(id+"F12.opPattern","COPY",FACE,{"derivedFrom":subQ5,"instanceName":"3"})]}),makeQuery(id+"F15.opExtrude","SWEPT_EDGE",EDGE,{"disambiguationData":[OSD([subQ3,subQ2,subQ1,subQ0]),TDD([makeQuery(id+"F12.opPattern","COPY",VERTEX,{"derivedFrom":makeQuery(id+"F11.opExtrude","CAP_VERTEX",VERTEX,{"disambiguationData":[OSD([subQ3,subQ2,subQ1,subQ0]),TDD([makeQuery(id+"F10.boolean.opBoolean","INTERSECT",VERTEX,{"derivedFrom":[subQ4,makeQuery(id+"F10.opExtrude","CAP_FACE",FACE,{"disambiguationData":[OSD([subQ2,subQ1,subQ0])],"isStart":true})]})])],"isStart":false}),"instanceName":"4"})])]})]});}
            var Q9;
            {var subQ0=sQuery(id+"F9.wireOp",EDGE,"E5");var subQ1=sQuery(id+"F9.wireOp",EDGE,"E4");var subQ2=sQuery(id+"F9.wireOp",EDGE,"E3");var subQ3=sQuery(id+"F0.wireOp",EDGE,"E1");var subQ4=makeQuery(id+"F4.boolean.opBoolean","MERGE",FACE,{"derivedFrom":[makeQuery(id+"F2.boolean.opBoolean","MERGE",FACE,{"derivedFrom":[makeQuery(id+"F1.opExtrude","SWEPT_FACE",FACE,{"disambiguationData":[OSD([subQ3])]}),makeQuery(id+"F2.opExtrude","SWEPT_FACE",FACE,{"disambiguationData":[OSD([subQ3])]})]}),makeQuery(id+"F4.opExtrude","SWEPT_FACE",FACE,{"disambiguationData":[OSD([subQ3])]})]});var subQ5=makeQuery(id+"F11.boolean.opBoolean","MERGE",FACE,{"derivedFrom":[subQ4,makeQuery(id+"F11.opExtrude","SWEPT_FACE",FACE,{"disambiguationData":[OSD([subQ3])]})]});Q9=makeQuery(id+"F15.boolean.opBoolean","MERGE",EDGE,{"derivedFrom":[makeQuery(id+"F13.opBoolean","INTERSECT",EDGE,{"disambiguationData":[OD(1.0)],"derivedFrom":[subQ5,makeQuery(id+"F12.opPattern","COPY",FACE,{"derivedFrom":subQ5,"instanceName":"1"}),makeQuery(id+"F12.opPattern","COPY",FACE,{"derivedFrom":subQ5,"instanceName":"2"}),makeQuery(id+"F12.opPattern","COPY",FACE,{"derivedFrom":subQ5,"instanceName":"4"})]}),makeQuery(id+"F15.opExtrude","SWEPT_EDGE",EDGE,{"disambiguationData":[OSD([subQ3,subQ2,subQ1,subQ0]),TDD([makeQuery(id+"F12.opPattern","COPY",VERTEX,{"derivedFrom":makeQuery(id+"F11.opExtrude","CAP_VERTEX",VERTEX,{"disambiguationData":[OSD([subQ3,subQ2,subQ1,subQ0]),TDD([makeQuery(id+"F10.boolean.opBoolean","INTERSECT",VERTEX,{"derivedFrom":[subQ4,makeQuery(id+"F10.opExtrude","CAP_FACE",FACE,{"disambiguationData":[OSD([subQ2,subQ1,subQ0])],"isStart":true})]})])],"isStart":false}),"instanceName":"3"})])]})]});}
            fillet(context, id + "F19", {"entities" : qUnion([Q0, Q1, Q2, Q3, Q4, Q5, Q6, Q7, Q8, Q9]), "radius" : 5.08 * mm, "tangentPropagation" : true, "allowEdgeOverflow" : false});
        }
    });
